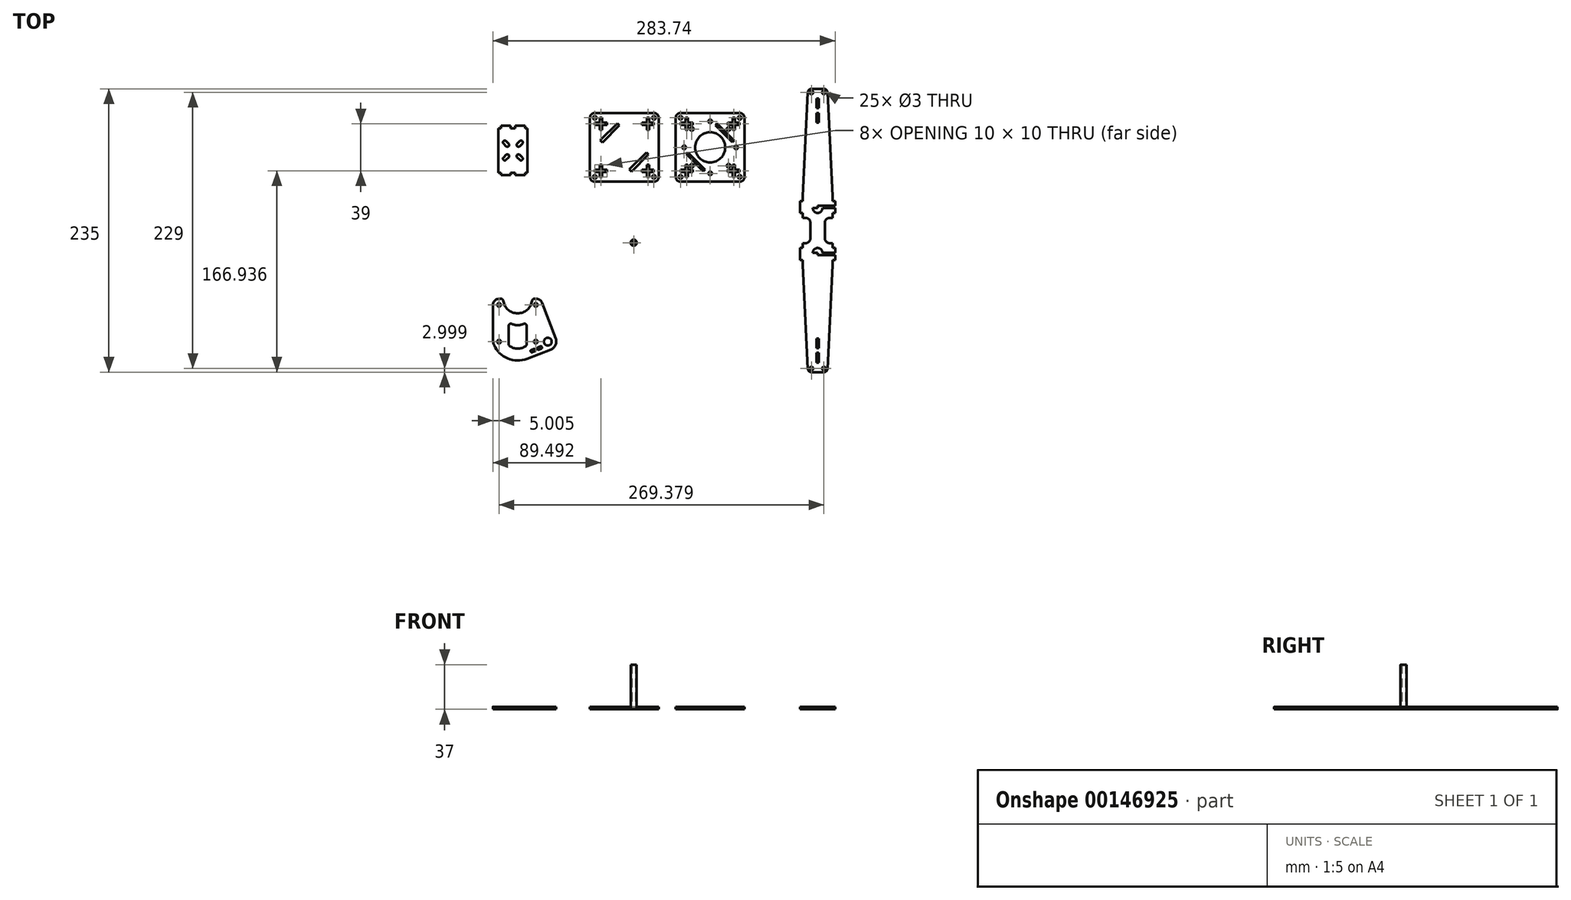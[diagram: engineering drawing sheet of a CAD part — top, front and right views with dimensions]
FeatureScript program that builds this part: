
annotation { "Feature Type Name" : "Feature", "Feature Type Description" : "" }
export const myFeature = defineFeature(function(context is Context, id is Id, definition is map)
    precondition{}
    {
        {
            var Q0;
            Q0=qCreatedBy(makeId("Top.planeOp"),FACE);
            var sketch = newSketch(context, id + "F0", { "sketchPlane" : qUnion([Q0])});
            skLineSegment(sketch, "E0", {"start": v(-188.84, 149.23) * mm, "end": v(-188.84, 112.23) * mm});
            skLineSegment(sketch, "E1", {"start": v(-188.84, 112.23) * mm, "end": v(-186.84, 112.23) * mm});
            skLineSegment(sketch, "E2", {"start": v(-186.84, 112.23) * mm, "end": v(-186.84, 110.23) * mm});
            skLineSegment(sketch, "E3", {"start": v(-186.84, 110.23) * mm, "end": v(-178.84, 110.23) * mm});
            skLineSegment(sketch, "E4", {"start": v(-178.84, 110.23) * mm, "end": v(-178.84, 112.23) * mm});
            skLineSegment(sketch, "E5", {"start": v(-178.84, 112.23) * mm, "end": v(-174.84, 112.23) * mm});
            skLineSegment(sketch, "E6", {"start": v(-174.84, 112.23) * mm, "end": v(-174.84, 110.23) * mm});
            skLineSegment(sketch, "E7", {"start": v(-174.84, 110.23) * mm, "end": v(-166.84, 110.23) * mm});
            skLineSegment(sketch, "E8", {"start": v(-166.84, 110.23) * mm, "end": v(-166.84, 112.23) * mm});
            skLineSegment(sketch, "E9", {"start": v(-166.84, 112.23) * mm, "end": v(-164.84, 112.23) * mm});
            skLineSegment(sketch, "E10", {"start": v(-164.84, 112.23) * mm, "end": v(-164.84, 149.23) * mm});
            skLineSegment(sketch, "E11", {"start": v(-164.84, 149.23) * mm, "end": v(-166.84, 149.23) * mm});
            skLineSegment(sketch, "E12", {"start": v(-166.84, 149.23) * mm, "end": v(-166.84, 151.23) * mm});
            skLineSegment(sketch, "E13", {"start": v(-166.84, 151.23) * mm, "end": v(-174.84, 151.23) * mm});
            skLineSegment(sketch, "E14", {"start": v(-174.84, 151.23) * mm, "end": v(-174.84, 149.23) * mm});
            skLineSegment(sketch, "E15", {"start": v(-174.84, 149.23) * mm, "end": v(-178.84, 149.23) * mm});
            skLineSegment(sketch, "E16", {"start": v(-178.84, 149.23) * mm, "end": v(-178.84, 151.23) * mm});
            skLineSegment(sketch, "E17", {"start": v(-178.84, 151.23) * mm, "end": v(-186.84, 151.23) * mm});
            skLineSegment(sketch, "E18", {"start": v(-186.84, 151.23) * mm, "end": v(-186.84, 149.23) * mm});
            skLineSegment(sketch, "E19", {"start": v(-186.84, 149.23) * mm, "end": v(-188.84, 149.23) * mm});
            skLineSegment(sketch, "E20", {"start": v(-188.84, 149.23) * mm, "end": v(-164.84, 112.23) * mm, "construction": true});
            skLineSegment(sketch, "E21", {"start": v(-164.84, 149.23) * mm, "end": v(-188.84, 112.23) * mm, "construction": true});
            skLineSegment(sketch, "E22", {"start": v(-176.84, 130.73) * mm, "end": v(-188.84, 130.73) * mm, "construction": true});
            skLineSegment(sketch, "E23", {"start": v(-176.84, 130.73) * mm, "end": v(-176.84, 149.23) * mm, "construction": true});
            skLineSegment(sketch, "E24", {"start": v(-185.74, 139.62) * mm, "end": v(-169.86, 123.75) * mm, "construction": true});
            skLineSegment(sketch, "E25", {"start": v(-169.19, 138.39) * mm, "end": v(-185.7, 121.88) * mm, "construction": true});
            skArc(sketch, "E26", {"start": v(-182.5, 134.27) * mm, "mid": v(-180.38, 134.27) * mm, "end": v(-180.38, 136.39) * mm});
            skArc(sketch, "E27", {"start": v(-182.49, 138.5) * mm, "mid": v(-184.62, 138.52) * mm, "end": v(-184.62, 136.39) * mm});
            skLineSegment(sketch, "E28", {"start": v(-182.51, 138.52) * mm, "end": v(-180.38, 136.39) * mm});
            skLineSegment(sketch, "E29", {"start": v(-180.38, 136.39) * mm, "end": v(-180.46, 136.3) * mm});
            skLineSegment(sketch, "E30", {"start": v(-182.5, 134.27) * mm, "end": v(-184.62, 136.39) * mm});
            skLineSegment(sketch, "E31.MirrorCS", {"start": v(-173.3, 136.39) * mm, "end": v(-173.23, 136.3) * mm});
            skLineSegment(sketch, "E32.MirrorCS", {"start": v(-171.19, 134.27) * mm, "end": v(-169.07, 136.39) * mm});
            skLineSegment(sketch, "E33.MirrorCS", {"start": v(-171.17, 138.52) * mm, "end": v(-173.3, 136.39) * mm});
            skArc(sketch, "E34.MirrorCS", {"start": v(-171.19, 134.27) * mm, "mid": v(-173.3, 134.27) * mm, "end": v(-173.3, 136.39) * mm});
            skArc(sketch, "E35.MirrorCS", {"start": v(-171.2, 138.5) * mm, "mid": v(-169.07, 138.52) * mm, "end": v(-169.07, 136.39) * mm});
            skLineSegment(sketch, "E36.MirrorCS", {"start": v(-173.3, 125.07) * mm, "end": v(-173.23, 125.16) * mm});
            skLineSegment(sketch, "E37.MirrorCS", {"start": v(-180.38, 125.07) * mm, "end": v(-180.46, 125.16) * mm});
            skArc(sketch, "E38.MirrorCS", {"start": v(-171.2, 122.97) * mm, "mid": v(-169.07, 122.95) * mm, "end": v(-169.07, 125.07) * mm});
            skLineSegment(sketch, "E39.MirrorCS", {"start": v(-182.5, 127.2) * mm, "end": v(-184.62, 125.07) * mm});
            skLineSegment(sketch, "E40.MirrorCS", {"start": v(-182.51, 122.94) * mm, "end": v(-180.38, 125.07) * mm});
            skArc(sketch, "E41.MirrorCS", {"start": v(-171.19, 127.2) * mm, "mid": v(-173.3, 127.2) * mm, "end": v(-173.3, 125.07) * mm});
            skArc(sketch, "E42.MirrorCS", {"start": v(-182.5, 127.2) * mm, "mid": v(-180.38, 127.2) * mm, "end": v(-180.38, 125.07) * mm});
            skArc(sketch, "E43.MirrorCS", {"start": v(-182.49, 122.97) * mm, "mid": v(-184.62, 122.95) * mm, "end": v(-184.62, 125.07) * mm});
            skLineSegment(sketch, "E44.MirrorCS", {"start": v(-171.19, 127.2) * mm, "end": v(-169.07, 125.07) * mm});
            skLineSegment(sketch, "E45.MirrorCS", {"start": v(-171.17, 122.94) * mm, "end": v(-173.3, 125.07) * mm});
            skSolve(sketch);
        }
        {
            var Q0;
            Q0 = qSketchRegion(id + "F0", true);
            extrude(context, id + "F1", {"entities" : qUnion([Q0]), "depth" : 2 * mm});
        }
        {
            var Q0;
            Q0=qCreatedBy(makeId("Top.planeOp"),FACE);
            var sketch = newSketch(context, id + "F2", { "sketchPlane" : qUnion([Q0])});
            skLineSegment(sketch, "E46.bottom", {"start": v(-108.9, 161.82) * mm, "end": v(-59.9, 161.82) * mm});
            skLineSegment(sketch, "E46.top", {"start": v(-108.9, 104.82) * mm, "end": v(-59.9, 104.82) * mm});
            skLineSegment(sketch, "E46.left", {"start": v(-112.9, 157.82) * mm, "end": v(-112.9, 108.82) * mm});
            skLineSegment(sketch, "E46.right", {"start": v(-55.9, 157.82) * mm, "end": v(-55.9, 108.82) * mm});
            skPoint(sketch, "E47.visualSharp", {"position": v(-112.9, 161.82) * mm});
            skArc(sketch, "E47.filletArc", {"start": v(-108.9, 161.82) * mm, "mid": v(-111.73, 160.64) * mm, "end": v(-112.9, 157.82) * mm});
            skPoint(sketch, "E48.visualSharp", {"position": v(-55.9, 161.82) * mm});
            skArc(sketch, "E48.filletArc", {"start": v(-55.9, 157.82) * mm, "mid": v(-57.07, 160.64) * mm, "end": v(-59.9, 161.82) * mm});
            skPoint(sketch, "E49.visualSharp", {"position": v(-55.9, 104.82) * mm});
            skArc(sketch, "E49.filletArc", {"start": v(-59.9, 104.82) * mm, "mid": v(-57.07, 105.99) * mm, "end": v(-55.9, 108.82) * mm});
            skPoint(sketch, "E50.visualSharp", {"position": v(-112.9, 104.82) * mm});
            skArc(sketch, "E50.filletArc", {"start": v(-112.9, 108.82) * mm, "mid": v(-111.73, 105.99) * mm, "end": v(-108.9, 104.82) * mm});
            skLineSegment(sketch, "E51", {"start": v(-104.9, 157.82) * mm, "end": v(-104.9, 153.82) * mm});
            skLineSegment(sketch, "E52", {"start": v(-104.9, 153.82) * mm, "end": v(-108.9, 153.82) * mm});
            skLineSegment(sketch, "E53", {"start": v(-108.9, 153.82) * mm, "end": v(-108.9, 151.82) * mm});
            skLineSegment(sketch, "E54", {"start": v(-108.9, 151.82) * mm, "end": v(-104.9, 151.82) * mm});
            skLineSegment(sketch, "E55", {"start": v(-104.9, 151.82) * mm, "end": v(-104.9, 147.82) * mm});
            skLineSegment(sketch, "E56", {"start": v(-104.9, 147.82) * mm, "end": v(-102.9, 147.82) * mm});
            skLineSegment(sketch, "E57", {"start": v(-102.9, 147.82) * mm, "end": v(-102.9, 151.82) * mm});
            skLineSegment(sketch, "E58", {"start": v(-102.9, 151.82) * mm, "end": v(-98.9, 151.82) * mm});
            skLineSegment(sketch, "E59", {"start": v(-98.9, 151.82) * mm, "end": v(-98.9, 153.82) * mm});
            skLineSegment(sketch, "E60", {"start": v(-98.9, 153.82) * mm, "end": v(-102.9, 153.82) * mm});
            skLineSegment(sketch, "E61", {"start": v(-102.9, 153.82) * mm, "end": v(-102.9, 157.82) * mm});
            skLineSegment(sketch, "E62", {"start": v(-102.9, 157.82) * mm, "end": v(-104.9, 157.82) * mm});
            skLineSegment(sketch, "E63", {"start": v(-84.4, 161.82) * mm, "end": v(-84.4, 104.82) * mm, "construction": true});
            skLineSegment(sketch, "E64", {"start": v(-55.9, 133.32) * mm, "end": v(-112.9, 133.32) * mm, "construction": true});
            skLineSegment(sketch, "E65.MirrorCS", {"start": v(-59.9, 153.82) * mm, "end": v(-59.9, 151.82) * mm});
            skLineSegment(sketch, "E66.MirrorCS", {"start": v(-69.9, 151.82) * mm, "end": v(-69.9, 153.82) * mm});
            skLineSegment(sketch, "E67.MirrorCS", {"start": v(-63.9, 147.82) * mm, "end": v(-65.9, 147.82) * mm});
            skLineSegment(sketch, "E68.MirrorCS", {"start": v(-65.9, 157.82) * mm, "end": v(-63.9, 157.82) * mm});
            skLineSegment(sketch, "E69.MirrorCS", {"start": v(-63.9, 157.82) * mm, "end": v(-63.9, 153.82) * mm});
            skLineSegment(sketch, "E70.MirrorCS", {"start": v(-63.9, 153.82) * mm, "end": v(-59.9, 153.82) * mm});
            skLineSegment(sketch, "E71.MirrorCS", {"start": v(-59.9, 151.82) * mm, "end": v(-63.9, 151.82) * mm});
            skLineSegment(sketch, "E72.MirrorCS", {"start": v(-63.9, 151.82) * mm, "end": v(-63.9, 147.82) * mm});
            skLineSegment(sketch, "E73.MirrorCS", {"start": v(-65.9, 153.82) * mm, "end": v(-65.9, 157.82) * mm});
            skLineSegment(sketch, "E74.MirrorCS", {"start": v(-65.9, 151.82) * mm, "end": v(-69.9, 151.82) * mm});
            skLineSegment(sketch, "E75.MirrorCS", {"start": v(-65.9, 147.82) * mm, "end": v(-65.9, 151.82) * mm});
            skLineSegment(sketch, "E76.MirrorCS", {"start": v(-69.9, 153.82) * mm, "end": v(-65.9, 153.82) * mm});
            skLineSegment(sketch, "E77.MirrorCS", {"start": v(-102.9, 108.82) * mm, "end": v(-104.9, 108.82) * mm});
            skLineSegment(sketch, "E78.MirrorCS", {"start": v(-59.9, 112.82) * mm, "end": v(-59.9, 114.82) * mm});
            skLineSegment(sketch, "E79.MirrorCS", {"start": v(-65.9, 108.82) * mm, "end": v(-63.9, 108.82) * mm});
            skLineSegment(sketch, "E80.MirrorCS", {"start": v(-108.9, 112.82) * mm, "end": v(-108.9, 114.82) * mm});
            skLineSegment(sketch, "E81.MirrorCS", {"start": v(-63.9, 118.82) * mm, "end": v(-65.9, 118.82) * mm});
            skLineSegment(sketch, "E82.MirrorCS", {"start": v(-98.9, 114.82) * mm, "end": v(-98.9, 112.82) * mm});
            skLineSegment(sketch, "E83.MirrorCS", {"start": v(-104.9, 118.82) * mm, "end": v(-102.9, 118.82) * mm});
            skLineSegment(sketch, "E84.MirrorCS", {"start": v(-69.9, 114.82) * mm, "end": v(-69.9, 112.82) * mm});
            skLineSegment(sketch, "E85.MirrorCS", {"start": v(-63.9, 108.82) * mm, "end": v(-63.9, 112.82) * mm});
            skLineSegment(sketch, "E86.MirrorCS", {"start": v(-102.9, 112.82) * mm, "end": v(-102.9, 108.82) * mm});
            skLineSegment(sketch, "E87.MirrorCS", {"start": v(-65.9, 114.82) * mm, "end": v(-69.9, 114.82) * mm});
            skLineSegment(sketch, "E88.MirrorCS", {"start": v(-104.9, 114.82) * mm, "end": v(-104.9, 118.82) * mm});
            skLineSegment(sketch, "E89.MirrorCS", {"start": v(-108.9, 114.82) * mm, "end": v(-104.9, 114.82) * mm});
            skLineSegment(sketch, "E90.MirrorCS", {"start": v(-104.9, 112.82) * mm, "end": v(-108.9, 112.82) * mm});
            skLineSegment(sketch, "E91.MirrorCS", {"start": v(-65.9, 112.82) * mm, "end": v(-65.9, 108.82) * mm});
            skLineSegment(sketch, "E92.MirrorCS", {"start": v(-69.9, 112.82) * mm, "end": v(-65.9, 112.82) * mm});
            skLineSegment(sketch, "E93.MirrorCS", {"start": v(-98.9, 112.82) * mm, "end": v(-102.9, 112.82) * mm});
            skLineSegment(sketch, "E94.MirrorCS", {"start": v(-104.9, 108.82) * mm, "end": v(-104.9, 112.82) * mm});
            skLineSegment(sketch, "E95.MirrorCS", {"start": v(-65.9, 118.82) * mm, "end": v(-65.9, 114.82) * mm});
            skLineSegment(sketch, "E96.MirrorCS", {"start": v(-59.9, 114.82) * mm, "end": v(-63.9, 114.82) * mm});
            skLineSegment(sketch, "E97.MirrorCS", {"start": v(-102.9, 114.82) * mm, "end": v(-98.9, 114.82) * mm});
            skLineSegment(sketch, "E98.MirrorCS", {"start": v(-63.9, 114.82) * mm, "end": v(-63.9, 118.82) * mm});
            skLineSegment(sketch, "E99.MirrorCS", {"start": v(-102.9, 118.82) * mm, "end": v(-102.9, 114.82) * mm});
            skLineSegment(sketch, "E100.MirrorCS", {"start": v(-63.9, 112.82) * mm, "end": v(-59.9, 112.82) * mm});
            skCircle(sketch, "E101", {"center": v(-108.9, 157.82) * mm, "radius": 1.5 * mm});
            skCircle(sketch, "E102.MirrorC", {"center": v(-59.9, 157.82) * mm, "radius": 1.5 * mm});
            skCircle(sketch, "E103.MirrorC", {"center": v(-108.9, 108.82) * mm, "radius": 1.5 * mm});
            skCircle(sketch, "E104.MirrorC", {"center": v(-59.9, 108.82) * mm, "radius": 1.5 * mm});
            skLineSegment(sketch, "E105", {"start": v(-84.4, 133.32) * mm, "end": v(-59.9, 157.82) * mm, "construction": true});
            skLineSegment(sketch, "E106", {"start": v(-48.84, 167.06) * mm, "end": v(-48.84, 103.7) * mm, "construction": true});
            skLineSegment(sketch, "E107.MirrorCS", {"start": v(-31.79, 108.82) * mm, "end": v(-33.79, 108.82) * mm});
            skLineSegment(sketch, "E108.MirrorCS", {"start": v(11.21, 112.82) * mm, "end": v(11.21, 114.82) * mm});
            skLineSegment(sketch, "E109.MirrorCS", {"start": v(-33.79, 118.82) * mm, "end": v(-31.79, 118.82) * mm});
            skLineSegment(sketch, "E110.MirrorCS", {"start": v(-37.79, 153.82) * mm, "end": v(-37.79, 151.82) * mm});
            skLineSegment(sketch, "E111.MirrorCS", {"start": v(1.21, 114.82) * mm, "end": v(1.21, 112.82) * mm});
            skLineSegment(sketch, "E112.MirrorCS", {"start": v(-27.79, 151.82) * mm, "end": v(-27.79, 153.82) * mm});
            skLineSegment(sketch, "E113.MirrorCS", {"start": v(5.21, 157.82) * mm, "end": v(7.21, 157.82) * mm});
            skLineSegment(sketch, "E114.MirrorCS", {"start": v(-37.79, 112.82) * mm, "end": v(-37.79, 114.82) * mm});
            skLineSegment(sketch, "E115.MirrorCS", {"start": v(11.21, 153.82) * mm, "end": v(11.21, 151.82) * mm});
            skLineSegment(sketch, "E116.MirrorCS", {"start": v(-27.79, 114.82) * mm, "end": v(-27.79, 112.82) * mm});
            skLineSegment(sketch, "E117.MirrorCS", {"start": v(-31.79, 157.82) * mm, "end": v(-33.79, 157.82) * mm});
            skLineSegment(sketch, "E118.MirrorCS", {"start": v(-33.79, 147.82) * mm, "end": v(-31.79, 147.82) * mm});
            skLineSegment(sketch, "E119.MirrorCS", {"start": v(7.21, 118.82) * mm, "end": v(5.21, 118.82) * mm});
            skLineSegment(sketch, "E120.MirrorCS", {"start": v(1.21, 151.82) * mm, "end": v(1.21, 153.82) * mm});
            skLineSegment(sketch, "E121.MirrorCS", {"start": v(7.21, 147.82) * mm, "end": v(5.21, 147.82) * mm});
            skLineSegment(sketch, "E122.MirrorCS", {"start": v(5.21, 108.82) * mm, "end": v(7.21, 108.82) * mm});
            skLineSegment(sketch, "E123.MirrorCS", {"start": v(1.21, 153.82) * mm, "end": v(5.21, 153.82) * mm});
            skCircle(sketch, "E124.MirrorC", {"center": v(-37.79, 157.82) * mm, "radius": 1.5 * mm});
            skLineSegment(sketch, "E125.MirrorCS", {"start": v(5.21, 112.82) * mm, "end": v(5.21, 108.82) * mm});
            skLineSegment(sketch, "E126.MirrorCS", {"start": v(-33.79, 153.82) * mm, "end": v(-37.79, 153.82) * mm});
            skLineSegment(sketch, "E127.MirrorCS", {"start": v(-33.79, 151.82) * mm, "end": v(-33.79, 147.82) * mm});
            skArc(sketch, "E128.MirrorCS", {"start": v(-37.79, 104.82) * mm, "mid": v(-40.62, 105.99) * mm, "end": v(-41.79, 108.82) * mm});
            skArc(sketch, "E129.MirrorCS", {"start": v(-41.79, 157.82) * mm, "mid": v(-40.62, 160.64) * mm, "end": v(-37.79, 161.82) * mm});
            skCircle(sketch, "E130.MirrorC", {"center": v(-37.79, 108.82) * mm, "radius": 1.5 * mm});
            skLineSegment(sketch, "E131.MirrorCS", {"start": v(7.21, 114.82) * mm, "end": v(7.21, 118.82) * mm});
            skLineSegment(sketch, "E132.MirrorCS", {"start": v(-31.79, 118.82) * mm, "end": v(-31.79, 114.82) * mm});
            skPoint(sketch, "E133.MirrorP", {"position": v(15.21, 104.82) * mm});
            skCircle(sketch, "E134.MirrorC", {"center": v(11.21, 108.82) * mm, "radius": 1.5 * mm});
            skLineSegment(sketch, "E135.MirrorCS", {"start": v(-31.79, 114.82) * mm, "end": v(-27.79, 114.82) * mm});
            skLineSegment(sketch, "E136.MirrorCS", {"start": v(-37.79, 151.82) * mm, "end": v(-33.79, 151.82) * mm});
            skLineSegment(sketch, "E137.MirrorCS", {"start": v(-31.79, 153.82) * mm, "end": v(-31.79, 157.82) * mm});
            skLineSegment(sketch, "E138.MirrorCS", {"start": v(-41.79, 133.32) * mm, "end": v(15.21, 133.32) * mm, "construction": true});
            skPoint(sketch, "E139.MirrorP", {"position": v(-41.79, 104.82) * mm});
            skLineSegment(sketch, "E140.MirrorCS", {"start": v(-13.29, 161.82) * mm, "end": v(-13.29, 104.82) * mm, "construction": true});
            skLineSegment(sketch, "E141.MirrorCS", {"start": v(-13.29, 133.32) * mm, "end": v(-37.79, 157.82) * mm, "construction": true});
            skLineSegment(sketch, "E142.MirrorCS", {"start": v(-37.79, 114.82) * mm, "end": v(-33.79, 114.82) * mm});
            skLineSegment(sketch, "E143.MirrorCS", {"start": v(11.21, 114.82) * mm, "end": v(7.21, 114.82) * mm});
            skArc(sketch, "E144.MirrorCS", {"start": v(15.21, 108.82) * mm, "mid": v(14.04, 105.99) * mm, "end": v(11.21, 104.82) * mm});
            skLineSegment(sketch, "E145.MirrorCS", {"start": v(7.21, 157.82) * mm, "end": v(7.21, 153.82) * mm});
            skLineSegment(sketch, "E146.MirrorCS", {"start": v(-31.79, 151.82) * mm, "end": v(-27.79, 151.82) * mm});
            skLineSegment(sketch, "E147.MirrorCS", {"start": v(5.21, 114.82) * mm, "end": v(1.21, 114.82) * mm});
            skLineSegment(sketch, "E148.MirrorCS", {"start": v(7.21, 112.82) * mm, "end": v(11.21, 112.82) * mm});
            skLineSegment(sketch, "E149.MirrorCS", {"start": v(-31.79, 112.82) * mm, "end": v(-31.79, 108.82) * mm});
            skLineSegment(sketch, "E150.MirrorCS", {"start": v(-33.79, 114.82) * mm, "end": v(-33.79, 118.82) * mm});
            skArc(sketch, "E151.MirrorCS", {"start": v(11.21, 161.82) * mm, "mid": v(14.04, 160.64) * mm, "end": v(15.21, 157.82) * mm});
            skLineSegment(sketch, "E152.MirrorCS", {"start": v(-41.79, 157.82) * mm, "end": v(-41.79, 108.82) * mm});
            skLineSegment(sketch, "E153.MirrorCS", {"start": v(15.21, 157.82) * mm, "end": v(15.21, 108.82) * mm});
            skLineSegment(sketch, "E154.MirrorCS", {"start": v(11.21, 104.82) * mm, "end": v(-37.79, 104.82) * mm});
            skLineSegment(sketch, "E155.MirrorCS", {"start": v(11.21, 161.82) * mm, "end": v(-37.79, 161.82) * mm});
            skLineSegment(sketch, "E156.MirrorCS", {"start": v(7.21, 108.82) * mm, "end": v(7.21, 112.82) * mm});
            skPoint(sketch, "E157.MirrorP", {"position": v(-41.79, 161.82) * mm});
            skLineSegment(sketch, "E158.MirrorCS", {"start": v(5.21, 151.82) * mm, "end": v(1.21, 151.82) * mm});
            skLineSegment(sketch, "E159.MirrorCS", {"start": v(-33.79, 157.82) * mm, "end": v(-33.79, 153.82) * mm});
            skLineSegment(sketch, "E160.MirrorCS", {"start": v(-33.79, 108.82) * mm, "end": v(-33.79, 112.82) * mm});
            skCircle(sketch, "E161.MirrorC", {"center": v(11.21, 157.82) * mm, "radius": 1.5 * mm});
            skLineSegment(sketch, "E162.MirrorCS", {"start": v(7.21, 153.82) * mm, "end": v(11.21, 153.82) * mm});
            skLineSegment(sketch, "E163.MirrorCS", {"start": v(-27.79, 153.82) * mm, "end": v(-31.79, 153.82) * mm});
            skLineSegment(sketch, "E164.MirrorCS", {"start": v(5.21, 118.82) * mm, "end": v(5.21, 114.82) * mm});
            skPoint(sketch, "E165.MirrorP", {"position": v(15.21, 161.82) * mm});
            skLineSegment(sketch, "E166.MirrorCS", {"start": v(11.21, 151.82) * mm, "end": v(7.21, 151.82) * mm});
            skLineSegment(sketch, "E167.MirrorCS", {"start": v(7.21, 151.82) * mm, "end": v(7.21, 147.82) * mm});
            skLineSegment(sketch, "E168.MirrorCS", {"start": v(5.21, 147.82) * mm, "end": v(5.21, 151.82) * mm});
            skLineSegment(sketch, "E169.MirrorCS", {"start": v(1.21, 112.82) * mm, "end": v(5.21, 112.82) * mm});
            skLineSegment(sketch, "E170.MirrorCS", {"start": v(-27.79, 112.82) * mm, "end": v(-31.79, 112.82) * mm});
            skLineSegment(sketch, "E171.MirrorCS", {"start": v(-33.79, 112.82) * mm, "end": v(-37.79, 112.82) * mm});
            skLineSegment(sketch, "E172.MirrorCS", {"start": v(5.21, 153.82) * mm, "end": v(5.21, 157.82) * mm});
            skLineSegment(sketch, "E173.MirrorCS", {"start": v(-31.79, 147.82) * mm, "end": v(-31.79, 151.82) * mm});
            skPoint(sketch, "E174.startSnap0", {"position": v(-98.9, 152.82) * mm});
            skLineSegment(sketch, "E175", {"start": v(-102.67, 137.44) * mm, "end": v(-88.52, 151.58) * mm});
            skLineSegment(sketch, "E176", {"start": v(-88.52, 151.58) * mm, "end": v(-90.3, 153.35) * mm});
            skLineSegment(sketch, "E177", {"start": v(-90.3, 153.35) * mm, "end": v(-104.43, 139.2) * mm});
            skLineSegment(sketch, "E178", {"start": v(-102.67, 137.44) * mm, "end": v(-104.43, 139.2) * mm});
            skLineSegment(sketch, "E179", {"start": v(-104.9, 153.82) * mm, "end": v(-84.4, 133.32) * mm, "construction": true});
            skLineSegment(sketch, "E180.MirrorCS", {"start": v(-66.13, 129.2) * mm, "end": v(-64.36, 127.42) * mm});
            skLineSegment(sketch, "E181.MirrorCS", {"start": v(-80.27, 115.05) * mm, "end": v(-66.13, 129.2) * mm});
            skLineSegment(sketch, "E182.MirrorCS", {"start": v(-80.27, 115.05) * mm, "end": v(-78.5, 113.28) * mm});
            skLineSegment(sketch, "E183.MirrorCS", {"start": v(-64.36, 127.42) * mm, "end": v(-78.5, 113.28) * mm});
            skPoint(sketch, "E184.orphan", {"position": v(-17.19, 158.43) * mm});
            skPoint(sketch, "E185.orphan", {"position": v(-38.4, 137.22) * mm});
            skPoint(sketch, "E186.orphan", {"position": v(-10.47, 109.29) * mm});
            skPoint(sketch, "E187.orphan", {"position": v(10.74, 130.5) * mm});
            skCircle(sketch, "E188", {"center": v(-13.29, 154.88) * mm, "radius": 1.5 * mm});
            skCircle(sketch, "E189.1.0", {"center": v(-34.86, 133.32) * mm, "radius": 1.5 * mm});
            skCircle(sketch, "E189.2.0", {"center": v(-13.29, 111.75) * mm, "radius": 1.5 * mm});
            skCircle(sketch, "E189.3.0", {"center": v(8.28, 133.32) * mm, "radius": 1.5 * mm});
            skPoint(sketch, "E189.center", {"position": v(-13.29, 133.32) * mm});
            skPoint(sketch, "E190.startSnap0", {"position": v(-31.79, 149.82) * mm});
            skPoint(sketch, "E190.endSnap0", {"position": v(3.21, 114.82) * mm});
            skLineSegment(sketch, "E191", {"start": v(-9.05, 151.7) * mm, "end": v(5.1, 137.56) * mm});
            skLineSegment(sketch, "E192", {"start": v(5.1, 137.56) * mm, "end": v(6.5, 138.97) * mm});
            skLineSegment(sketch, "E193", {"start": v(6.5, 138.97) * mm, "end": v(-7.63, 153.12) * mm});
            skLineSegment(sketch, "E194", {"start": v(-7.63, 153.12) * mm, "end": v(-9.05, 151.7) * mm});
            skLineSegment(sketch, "E195.MirrorCS", {"start": v(-17.53, 114.93) * mm, "end": v(-18.95, 113.52) * mm});
            skLineSegment(sketch, "E196.MirrorCS", {"start": v(-18.95, 113.52) * mm, "end": v(-33.09, 127.66) * mm});
            skLineSegment(sketch, "E197.MirrorCS", {"start": v(-33.09, 127.66) * mm, "end": v(-31.67, 129.07) * mm});
            skLineSegment(sketch, "E198.MirrorCS", {"start": v(-31.67, 129.07) * mm, "end": v(-17.53, 114.93) * mm});
            skCircle(sketch, "E199", {"center": v(-28.54, 148.57) * mm, "radius": 1.5 * mm});
            skCircle(sketch, "E200.1.0", {"center": v(-28.54, 118.07) * mm, "radius": 1.5 * mm});
            skCircle(sketch, "E200.2.0", {"center": v(1.96, 118.07) * mm, "radius": 1.5 * mm});
            skCircle(sketch, "E200.3.0", {"center": v(1.96, 148.57) * mm, "radius": 1.5 * mm});
            skCircle(sketch, "E201", {"center": v(-13.29, 133.32) * mm, "radius": 12.5 * mm});
            skSolve(sketch);
        }
        {
            var Q0;
            Q0 = qSketchRegion(id + "F2", true);
            extrude(context, id + "F3", {"entities" : qUnion([Q0]), "depth" : 2 * mm});
        }
        {
            var Q0;
            Q0=qCreatedBy(makeId("Top.planeOp"),FACE);
            var sketch = newSketch(context, id + "F4", { "sketchPlane" : qUnion([Q0])});
            skLineSegment(sketch, "E202.bottom", {"start": v(70.7, 181.88) * mm, "end": v(81, 181.88) * mm});
            skLineSegment(sketch, "E202.top", {"start": v(70.7, -53.12) * mm, "end": v(81, -53.12) * mm});
            skLineSegment(sketch, "E202.left", {"start": v(61.35, 88.88) * mm, "end": v(61.35, 78.88) * mm});
            skLineSegment(sketch, "E202.right", {"start": v(90.35, 88.88) * mm, "end": v(90.35, 84.88) * mm});
            skLineSegment(sketch, "E203", {"start": v(61.35, 78.88) * mm, "end": v(63.35, 78.88) * mm});
            skLineSegment(sketch, "E204", {"start": v(63.35, 78.88) * mm, "end": v(63.35, 74.88) * mm});
            skLineSegment(sketch, "E205", {"start": v(63.35, 49.88) * mm, "end": v(61.35, 49.88) * mm});
            skLineSegment(sketch, "E206", {"start": v(61.35, 64.38) * mm, "end": v(101.5, 64.38) * mm, "construction": true});
            skPoint(sketch, "E206.endSnap0", {"position": v(90.35, 64.38) * mm});
            skLineSegment(sketch, "E207", {"start": v(63.35, 49.88) * mm, "end": v(63.35, 53.88) * mm});
            skLineSegment(sketch, "E208", {"start": v(63.35, 74.88) * mm, "end": v(65.85, 74.88) * mm});
            skLineSegment(sketch, "E209", {"start": v(69.85, 70.88) * mm, "end": v(69.85, 57.88) * mm});
            skLineSegment(sketch, "E210", {"start": v(65.85, 53.88) * mm, "end": v(63.35, 53.88) * mm});
            skPoint(sketch, "E211.visualSharp", {"position": v(69.85, 74.88) * mm});
            skArc(sketch, "E211.filletArc", {"start": v(69.85, 70.88) * mm, "mid": v(68.67, 73.7) * mm, "end": v(65.85, 74.88) * mm});
            skPoint(sketch, "E212.visualSharp", {"position": v(69.85, 53.88) * mm});
            skArc(sketch, "E212.filletArc", {"start": v(65.85, 53.88) * mm, "mid": v(68.67, 55.05) * mm, "end": v(69.85, 57.88) * mm});
            skLineSegment(sketch, "E213.trimOffspring", {"start": v(61.35, 49.88) * mm, "end": v(61.35, 39.88) * mm});
            skLineSegment(sketch, "E214", {"start": v(75.85, 181.88) * mm, "end": v(75.85, -53.12) * mm, "construction": true});
            skLineSegment(sketch, "E215.MirrorCS", {"start": v(88.35, 49.88) * mm, "end": v(90.35, 49.88) * mm});
            skLineSegment(sketch, "E216.MirrorCS", {"start": v(90.35, 78.88) * mm, "end": v(88.35, 78.88) * mm});
            skPoint(sketch, "E217.MirrorP", {"position": v(81.85, 74.88) * mm});
            skPoint(sketch, "E218.MirrorP", {"position": v(81.85, 53.88) * mm});
            skLineSegment(sketch, "E219.MirrorCS", {"start": v(85.85, 53.88) * mm, "end": v(88.35, 53.88) * mm});
            skArc(sketch, "E220.MirrorCS", {"start": v(81.85, 70.88) * mm, "mid": v(83.02, 73.7) * mm, "end": v(85.85, 74.88) * mm});
            skLineSegment(sketch, "E221.MirrorCS", {"start": v(81.85, 70.88) * mm, "end": v(81.85, 57.88) * mm});
            skArc(sketch, "E222.MirrorCS", {"start": v(85.85, 53.88) * mm, "mid": v(83.02, 55.05) * mm, "end": v(81.85, 57.88) * mm});
            skLineSegment(sketch, "E223.MirrorCS", {"start": v(88.35, 49.88) * mm, "end": v(88.35, 53.88) * mm});
            skLineSegment(sketch, "E224.MirrorCS", {"start": v(88.35, 74.88) * mm, "end": v(85.85, 74.88) * mm});
            skLineSegment(sketch, "E225.MirrorCS", {"start": v(88.35, 78.88) * mm, "end": v(88.35, 74.88) * mm});
            skLineSegment(sketch, "E226.trimOffspring", {"start": v(90.35, 49.88) * mm, "end": v(90.35, 45.88) * mm});
            skLineSegment(sketch, "E227", {"start": v(61.35, 88.88) * mm, "end": v(63.35, 88.88) * mm});
            skLineSegment(sketch, "E228", {"start": v(63.35, 88.88) * mm, "end": v(63.35, 92.88) * mm});
            skLineSegment(sketch, "E229", {"start": v(63.35, 92.88) * mm, "end": v(67.7, 179.03) * mm});
            skPoint(sketch, "E230.orphan", {"position": v(61.35, 181.88) * mm});
            skLineSegment(sketch, "E231.MirrorCS", {"start": v(88.35, 92.88) * mm, "end": v(83.99, 179.03) * mm});
            skLineSegment(sketch, "E232.MirrorCS", {"start": v(88.35, 88.88) * mm, "end": v(88.35, 92.88) * mm});
            skLineSegment(sketch, "E233.MirrorCS", {"start": v(90.35, 88.88) * mm, "end": v(88.35, 88.88) * mm});
            skPoint(sketch, "E234.orphan", {"position": v(90.35, 181.88) * mm});
            skLineSegment(sketch, "E235.MirrorCS", {"start": v(61.35, 39.88) * mm, "end": v(63.35, 39.88) * mm});
            skLineSegment(sketch, "E236.MirrorCS", {"start": v(63.35, 39.88) * mm, "end": v(63.35, 35.88) * mm});
            skLineSegment(sketch, "E237.MirrorCS", {"start": v(90.35, 39.88) * mm, "end": v(88.35, 39.88) * mm});
            skLineSegment(sketch, "E238.MirrorCS", {"start": v(88.35, 39.88) * mm, "end": v(88.35, 35.88) * mm});
            skLineSegment(sketch, "E239.MirrorCS", {"start": v(88.35, 35.88) * mm, "end": v(83.99, -50.27) * mm});
            skLineSegment(sketch, "E240.MirrorCS", {"start": v(63.35, 35.88) * mm, "end": v(67.7, -50.27) * mm});
            skPoint(sketch, "E241.MirrorP", {"position": v(61.35, -53.12) * mm});
            skPoint(sketch, "E242.MirrorP", {"position": v(90.35, -53.12) * mm});
            skPoint(sketch, "E243.visualSharp", {"position": v(67.85, 181.88) * mm});
            skArc(sketch, "E243.filletArc", {"start": v(70.7, 181.88) * mm, "mid": v(68.63, 181.05) * mm, "end": v(67.7, 179.03) * mm});
            skPoint(sketch, "E244.visualSharp", {"position": v(83.85, 181.88) * mm});
            skArc(sketch, "E244.filletArc", {"start": v(83.99, 179.03) * mm, "mid": v(83.06, 181.05) * mm, "end": v(81, 181.88) * mm});
            skPoint(sketch, "E245.visualSharp", {"position": v(83.85, -53.12) * mm});
            skArc(sketch, "E245.filletArc", {"start": v(81, -53.12) * mm, "mid": v(83.06, -52.3) * mm, "end": v(83.99, -50.27) * mm});
            skPoint(sketch, "E246.visualSharp", {"position": v(67.85, -53.12) * mm});
            skArc(sketch, "E246.filletArc", {"start": v(67.7, -50.27) * mm, "mid": v(68.63, -52.3) * mm, "end": v(70.7, -53.12) * mm});
            skLineSegment(sketch, "E247", {"start": v(90.35, 84.88) * mm, "end": v(75.85, 84.88) * mm});
            skLineSegment(sketch, "E248", {"start": v(75.85, 84.88) * mm, "end": v(75.85, 82.88) * mm});
            skLineSegment(sketch, "E249", {"start": v(75.85, 82.88) * mm, "end": v(71.85, 82.88) * mm});
            skLineSegment(sketch, "E250", {"start": v(90.35, 82.88) * mm, "end": v(79.85, 82.88) * mm});
            skArc(sketch, "E251", {"start": v(71.85, 82.88) * mm, "mid": v(75.85, 78.88) * mm, "end": v(79.85, 82.88) * mm});
            skLineSegment(sketch, "E252.trimOffspring", {"start": v(90.35, 82.88) * mm, "end": v(90.35, 78.88) * mm});
            skLineSegment(sketch, "E253.MirrorCS", {"start": v(90.35, 43.88) * mm, "end": v(75.85, 43.88) * mm});
            skLineSegment(sketch, "E254.MirrorCS", {"start": v(75.85, 45.88) * mm, "end": v(71.85, 45.88) * mm});
            skLineSegment(sketch, "E255.MirrorCS", {"start": v(75.85, 43.88) * mm, "end": v(75.85, 45.88) * mm});
            skArc(sketch, "E256.MirrorCS", {"start": v(71.85, 45.88) * mm, "mid": v(75.85, 49.88) * mm, "end": v(79.85, 45.88) * mm});
            skLineSegment(sketch, "E257.MirrorCS", {"start": v(90.35, 45.88) * mm, "end": v(79.85, 45.88) * mm});
            skLineSegment(sketch, "E258.trimOffspring", {"start": v(90.35, 43.88) * mm, "end": v(90.35, 39.88) * mm});
            skLineSegment(sketch, "E259.bottom", {"start": v(74.85, 173.88) * mm, "end": v(76.85, 173.88) * mm});
            skLineSegment(sketch, "E259.top", {"start": v(74.85, 165.88) * mm, "end": v(76.85, 165.88) * mm});
            skLineSegment(sketch, "E259.left", {"start": v(74.85, 173.88) * mm, "end": v(74.85, 165.88) * mm});
            skLineSegment(sketch, "E259.right", {"start": v(76.85, 173.88) * mm, "end": v(76.85, 165.88) * mm});
            skLineSegment(sketch, "E260.bottom", {"start": v(74.85, 161.88) * mm, "end": v(76.85, 161.88) * mm});
            skLineSegment(sketch, "E260.top", {"start": v(74.85, 153.88) * mm, "end": v(76.85, 153.88) * mm});
            skLineSegment(sketch, "E260.left", {"start": v(74.85, 161.88) * mm, "end": v(74.85, 153.88) * mm});
            skLineSegment(sketch, "E260.right", {"start": v(76.85, 161.88) * mm, "end": v(76.85, 153.88) * mm});
            skCircle(sketch, "E261", {"center": v(81, 178.88) * mm, "radius": 1.5 * mm});
            skCircle(sketch, "E262", {"center": v(70.7, 178.88) * mm, "radius": 1.5 * mm});
            skLineSegment(sketch, "E263.MirrorCS", {"start": v(74.85, -45.12) * mm, "end": v(76.85, -45.12) * mm});
            skLineSegment(sketch, "E264.MirrorCS", {"start": v(74.85, -45.12) * mm, "end": v(74.85, -37.12) * mm});
            skLineSegment(sketch, "E265.MirrorCS", {"start": v(74.85, -37.12) * mm, "end": v(76.85, -37.12) * mm});
            skLineSegment(sketch, "E266.MirrorCS", {"start": v(74.85, -33.12) * mm, "end": v(74.85, -25.12) * mm});
            skLineSegment(sketch, "E267.MirrorCS", {"start": v(76.85, -45.12) * mm, "end": v(76.85, -37.12) * mm});
            skLineSegment(sketch, "E268.MirrorCS", {"start": v(74.85, -33.12) * mm, "end": v(76.85, -33.12) * mm});
            skLineSegment(sketch, "E269.MirrorCS", {"start": v(76.85, -33.12) * mm, "end": v(76.85, -25.12) * mm});
            skLineSegment(sketch, "E270.MirrorCS", {"start": v(74.85, -25.12) * mm, "end": v(76.85, -25.12) * mm});
            skCircle(sketch, "E271.MirrorC", {"center": v(81, -50.12) * mm, "radius": 1.5 * mm});
            skCircle(sketch, "E272.MirrorC", {"center": v(70.7, -50.12) * mm, "radius": 1.5 * mm});
            skSolve(sketch);
        }
        {
            var Q0;
            Q0 = qSketchRegion(id + "F4", true);
            extrude(context, id + "F5", {"entities" : qUnion([Q0]), "depth" : 2 * mm});
        }
        {
            var Q0;
            Q0=qCreatedBy(makeId("Top.planeOp"),FACE);
            var sketch = newSketch(context, id + "F6", { "sketchPlane" : qUnion([Q0])});
            skLineSegment(sketch, "E273.bottom", {"start": v(-188.39, 7.7) * mm, "end": v(-186.74, 7.7) * mm});
            skLineSegment(sketch, "E273.left", {"start": v(-193.39, 2.7) * mm, "end": v(-193.39, -26.55) * mm});
            skCircle(sketch, "E274", {"center": v(-188.39, 2.7) * mm, "radius": 1.5 * mm});
            skCircle(sketch, "E275", {"center": v(-157.89, 2.7) * mm, "radius": 1.5 * mm});
            skCircle(sketch, "E276", {"center": v(-188.39, -27.8) * mm, "radius": 1.5 * mm});
            skCircle(sketch, "E277", {"center": v(-157.89, -27.8) * mm, "radius": 1.5 * mm});
            skPoint(sketch, "E278.visualSharp", {"position": v(-193.39, 7.7) * mm});
            skArc(sketch, "E278.filletArc", {"start": v(-188.39, 7.7) * mm, "mid": v(-191.92, 6.24) * mm, "end": v(-193.39, 2.7) * mm});
            skPoint(sketch, "E279.visualSharp", {"position": v(-152.39, 7.7) * mm});
            skArc(sketch, "E279.filletArc", {"start": v(-152.71, 4.5) * mm, "mid": v(-154.55, 6.83) * mm, "end": v(-157.39, 7.7) * mm});
            skPoint(sketch, "E280.visualSharp", {"position": v(-152.39, -33.3) * mm});
            skPoint(sketch, "E281.visualSharp", {"position": v(-193.39, -33.3) * mm});
            skArc(sketch, "E282", {"start": v(-184.76, 6) * mm, "mid": v(-172.89, -4.3) * mm, "end": v(-161, 6) * mm});
            skLineSegment(sketch, "E283.trimOffspring", {"start": v(-159.03, 7.7) * mm, "end": v(-157.39, 7.7) * mm});
            skPoint(sketch, "E284.visualSharp", {"position": v(-184.89, 7.7) * mm});
            skArc(sketch, "E284.filletArc", {"start": v(-184.76, 6) * mm, "mid": v(-185.43, 7.22) * mm, "end": v(-186.74, 7.7) * mm});
            skPoint(sketch, "E285.visualSharp", {"position": v(-160.89, 7.7) * mm});
            skArc(sketch, "E285.filletArc", {"start": v(-159.03, 7.7) * mm, "mid": v(-160.34, 7.22) * mm, "end": v(-161, 6) * mm});
            skArc(sketch, "E286", {"start": v(-192.56, -30.53) * mm, "mid": v(-181.15, -41.79) * mm, "end": v(-165.13, -42) * mm});
            skPoint(sketch, "E286.centerSnap0", {"position": v(-172.89, -33.3) * mm});
            skPoint(sketch, "E287.orphan", {"position": v(-157.39, -33.3) * mm});
            skPoint(sketch, "E288.orphan", {"position": v(-188.39, -33.3) * mm});
            skPoint(sketch, "E289.visualSharp", {"position": v(-193.39, -28.3) * mm});
            skArc(sketch, "E289.filletArc", {"start": v(-193.39, -26.55) * mm, "mid": v(-193.18, -28.58) * mm, "end": v(-192.56, -30.53) * mm});
            skPoint(sketch, "E290.visualSharp", {"position": v(-152.39, -28.3) * mm});
            skLineSegment(sketch, "E291.left", {"start": v(-180.39, -14.86) * mm, "end": v(-180.39, -29.8) * mm});
            skLineSegment(sketch, "E291.right", {"start": v(-165.39, -14.86) * mm, "end": v(-165.39, -29.8) * mm});
            skArc(sketch, "E292", {"start": v(-177.46, -13.09) * mm, "mid": v(-172.89, -14.2) * mm, "end": v(-168.3, -13.09) * mm});
            skArc(sketch, "E293", {"start": v(-179.54, -31.44) * mm, "mid": v(-172.89, -33.55) * mm, "end": v(-166.23, -31.44) * mm});
            skPoint(sketch, "E294.visualSharp", {"position": v(-180.39, -10.78) * mm});
            skArc(sketch, "E294.filletArc", {"start": v(-177.46, -13.09) * mm, "mid": v(-179.42, -13.15) * mm, "end": v(-180.39, -14.86) * mm});
            skPoint(sketch, "E295.visualSharp", {"position": v(-165.39, -10.78) * mm});
            skArc(sketch, "E295.filletArc", {"start": v(-165.39, -14.86) * mm, "mid": v(-166.35, -13.15) * mm, "end": v(-168.3, -13.09) * mm});
            skPoint(sketch, "E296.visualSharp", {"position": v(-165.39, -30.78) * mm});
            skArc(sketch, "E296.filletArc", {"start": v(-166.23, -31.44) * mm, "mid": v(-165.6, -30.72) * mm, "end": v(-165.39, -29.8) * mm});
            skPoint(sketch, "E297.visualSharp", {"position": v(-180.39, -30.78) * mm});
            skArc(sketch, "E297.filletArc", {"start": v(-180.39, -29.8) * mm, "mid": v(-180.16, -30.72) * mm, "end": v(-179.54, -31.44) * mm});
            skCircle(sketch, "E298", {"center": v(-147.89, -27.8) * mm, "radius": 3.25 * mm});
            skArc(sketch, "E299", {"start": v(-145.35, -34.32) * mm, "mid": v(-141.49, -30.63) * mm, "end": v(-141.35, -25.3) * mm});
            skLineSegment(sketch, "E300", {"start": v(-145.35, -34.32) * mm, "end": v(-165.13, -42) * mm});
            skLineSegment(sketch, "E301", {"start": v(-141.35, -25.3) * mm, "end": v(-152.71, 4.5) * mm});
            skLineSegment(sketch, "E302", {"start": v(-153.13, -33.58) * mm, "end": v(-155.37, -34.45) * mm});
            skLineSegment(sketch, "E303", {"start": v(-162, -36.16) * mm, "end": v(-162.14, -35.8) * mm});
            skLineSegment(sketch, "E304", {"start": v(-161.69, -34.76) * mm, "end": v(-159.45, -33.89) * mm});
            skLineSegment(sketch, "E305", {"start": v(-152.82, -32.17) * mm, "end": v(-152.67, -32.55) * mm});
            skLineSegment(sketch, "E306", {"start": v(-158.41, -34.34) * mm, "end": v(-158.27, -34.72) * mm});
            skLineSegment(sketch, "E307", {"start": v(-156.55, -33.62) * mm, "end": v(-156.4, -34) * mm});
            skLineSegment(sketch, "E308.trimOffspring", {"start": v(-156.1, -32.59) * mm, "end": v(-153.85, -31.72) * mm});
            skLineSegment(sketch, "E309.trimOffspring", {"start": v(-158.72, -35.75) * mm, "end": v(-160.96, -36.62) * mm});
            skPoint(sketch, "E310.visualSharp", {"position": v(-162.43, -35.05) * mm});
            skArc(sketch, "E310.filletArc", {"start": v(-161.69, -34.76) * mm, "mid": v(-162.13, -35.18) * mm, "end": v(-162.14, -35.8) * mm});
            skPoint(sketch, "E311.visualSharp", {"position": v(-161.7, -36.91) * mm});
            skArc(sketch, "E311.filletArc", {"start": v(-162, -36.16) * mm, "mid": v(-161.57, -36.6) * mm, "end": v(-160.96, -36.62) * mm});
            skPoint(sketch, "E312.visualSharp", {"position": v(-157.98, -35.46) * mm});
            skArc(sketch, "E312.filletArc", {"start": v(-158.72, -35.75) * mm, "mid": v(-158.28, -35.33) * mm, "end": v(-158.27, -34.72) * mm});
            skPoint(sketch, "E313.visualSharp", {"position": v(-158.7, -33.6) * mm});
            skArc(sketch, "E313.filletArc", {"start": v(-158.41, -34.34) * mm, "mid": v(-158.84, -33.9) * mm, "end": v(-159.45, -33.89) * mm});
            skPoint(sketch, "E314.visualSharp", {"position": v(-156.84, -32.88) * mm});
            skArc(sketch, "E314.filletArc", {"start": v(-156.1, -32.59) * mm, "mid": v(-156.53, -33) * mm, "end": v(-156.55, -33.62) * mm});
            skPoint(sketch, "E315.visualSharp", {"position": v(-153.1, -31.43) * mm});
            skArc(sketch, "E315.filletArc", {"start": v(-152.82, -32.17) * mm, "mid": v(-153.24, -31.73) * mm, "end": v(-153.85, -31.72) * mm});
            skArc(sketch, "E316.filletArc", {"start": v(-153.13, -33.58) * mm, "mid": v(-152.69, -33.16) * mm, "end": v(-152.67, -32.55) * mm});
            skPoint(sketch, "E317.visualSharp", {"position": v(-156.11, -34.74) * mm});
            skArc(sketch, "E317.filletArc", {"start": v(-156.4, -34) * mm, "mid": v(-155.98, -34.44) * mm, "end": v(-155.37, -34.45) * mm});
            skSolve(sketch);
        }
        {
            var Q0;
            Q0=makeQuery(id+"F6.imprint","IMPRINT",FACE,{"disambiguationData":[TD([[makeQuery(id+"F6.imprint","IMPRINT",EDGE,{"derivedFrom":sQuery(id+"F6.wireOp",EDGE,"E273.bottom")}),-1.0]])]});
            extrude(context, id + "F7", {"entities" : qUnion([Q0]), "depth" : 2 * mm});
        }
        {
            var Q0;
            Q0=qCreatedBy(makeId("Top.planeOp"),FACE);
            var sketch = newSketch(context, id + "F8", { "sketchPlane" : qUnion([Q0])});
            skCircle(sketch, "E318", {"center": v(-76.7, 54.28) * mm, "radius": 2.5 * mm});
            skCircle(sketch, "E319", {"center": v(-76.7, 54.28) * mm, "radius": 1.5 * mm});
            skSolve(sketch);
        }
        {
            var Q0;
            Q0 = qSketchRegion(id + "F8", true);
            extrude(context, id + "F9", {"entities" : qUnion([Q0]), "depth" : 37 * mm});
        }
    });
